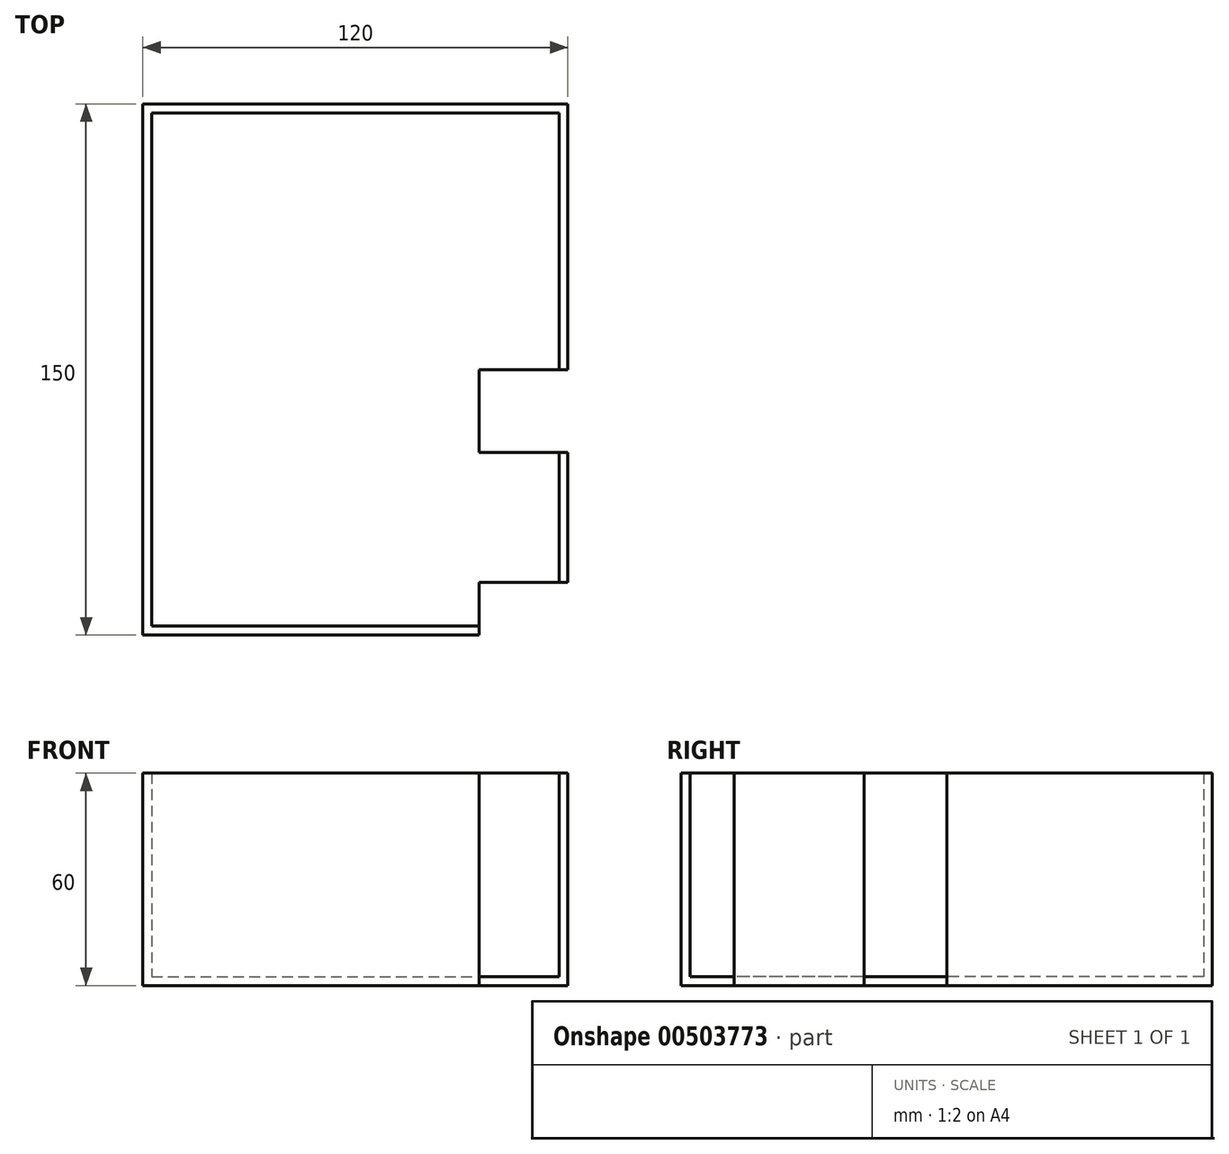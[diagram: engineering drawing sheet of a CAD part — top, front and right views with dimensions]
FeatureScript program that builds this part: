
annotation { "Feature Type Name" : "Feature", "Feature Type Description" : "" }
export const myFeature = defineFeature(function(context is Context, id is Id, definition is map)
    precondition{}
    {
        {
            var Q0;
            Q0=qCreatedBy(makeId("Top.planeOp"),FACE);
            var sketch = newSketch(context, id + "F0", { "sketchPlane" : qUnion([Q0])});
            skLineSegment(sketch, "E0.bottom", {"start": v(-60, 75) * mm, "end": v(60, 75) * mm});
            skLineSegment(sketch, "E0.top", {"start": v(-60, -75) * mm, "end": v(60, -75) * mm});
            skLineSegment(sketch, "E0.left", {"start": v(-60, 75) * mm, "end": v(-60, -75) * mm});
            skLineSegment(sketch, "E0.right", {"start": v(60, 75) * mm, "end": v(60, -75) * mm});
            skPoint(sketch, "E0.middle", {"position": v(0, 0) * mm});
            skSolve(sketch);
        }
        {
            var Q0;
            Q0 = qSketchRegion(id + "F0", true);
            extrude(context, id + "F1", {"entities" : qUnion([Q0]), "depth" : 60 * mm});
        }
        {
            var Q0;
            Q0=makeQuery(id+"F1.opExtrude","CAP_FACE",FACE,{"disambiguationData":[OSD([sQuery(id+"F0.wireOp",EDGE,"E0.bottom"),sQuery(id+"F0.wireOp",EDGE,"E0.top"),sQuery(id+"F0.wireOp",EDGE,"E0.left"),sQuery(id+"F0.wireOp",EDGE,"E0.right")])],"isStart":false});
            shell(context, id + "F2", {"entities" : qUnion([Q0]), "thickness" : 2.5 * mm});
        }
        {
            var Q0;
            Q0=makeQuery(id+"F1.opExtrude","SWEPT_FACE",FACE,{"disambiguationData":[OSD([sQuery(id+"F0.wireOp",EDGE,"E0.right")])]});
            var sketch = newSketch(context, id + "F3", { "sketchPlane" : qUnion([Q0])});
            skLineSegment(sketch, "E1.bottom", {"start": v(-82, 0) * mm, "end": v(-60.1, 0) * mm});
            skLineSegment(sketch, "E1.top", {"start": v(-82, 60) * mm, "end": v(-60.1, 60) * mm});
            skLineSegment(sketch, "E1.left", {"start": v(-82, 0) * mm, "end": v(-82, 60) * mm});
            skLineSegment(sketch, "E1.right", {"start": v(-60.1, 0) * mm, "end": v(-60.1, 60) * mm});
            skSolve(sketch);
        }
        {
            var Q0;
            Q0=makeQuery(id+"F3.imprint","IMPRINT",FACE,{"disambiguationData":[TD([[makeQuery(id+"F3.imprint","IMPRINT",EDGE,{"derivedFrom":sQuery(id+"F3.wireOp",EDGE,"E1.bottom")}),-1.0]])]});
            extrude(context, id + "F4", {"entities" : qUnion([Q0]), "operationType" : NewBodyOperationType.REMOVE, "oppositeDirection" : true, "depth" : 25 * mm});
        }
        {
            var Q0;
            {var subQ0=sQuery(id+"F0.wireOp",EDGE,"E0.bottom");var subQ1=sQuery(id+"F0.wireOp",EDGE,"E0.right");Q0=makeQuery(id+"F4.boolean.opBoolean","SPLIT",FACE,{"disambiguationData":[TD([makeQuery(id+"F1.opExtrude","SWEPT_FACE",FACE,{"disambiguationData":[OSD([subQ0])]})])],"derivedFrom":makeQuery(id+"F1.opExtrude","SWEPT_FACE",FACE,{"disambiguationData":[OSD([subQ1])]})});}
            var sketch = newSketch(context, id + "F5", { "sketchPlane" : qUnion([Q0])});
            skLineSegment(sketch, "E2.bottom", {"start": v(-23.39, 0) * mm, "end": v(0, 0) * mm});
            skLineSegment(sketch, "E2.top", {"start": v(-23.39, 60) * mm, "end": v(0, 60) * mm});
            skLineSegment(sketch, "E2.left", {"start": v(-23.39, 0) * mm, "end": v(-23.39, 60) * mm});
            skLineSegment(sketch, "E2.right", {"start": v(0, 0) * mm, "end": v(0, 60) * mm});
            skSolve(sketch);
        }
        {
            var Q0;
            Q0 = qSketchRegion(id + "F5", true);
            extrude(context, id + "F6", {"entities" : qUnion([Q0]), "operationType" : NewBodyOperationType.REMOVE, "oppositeDirection" : true, "depth" : 25 * mm});
        }
    });
